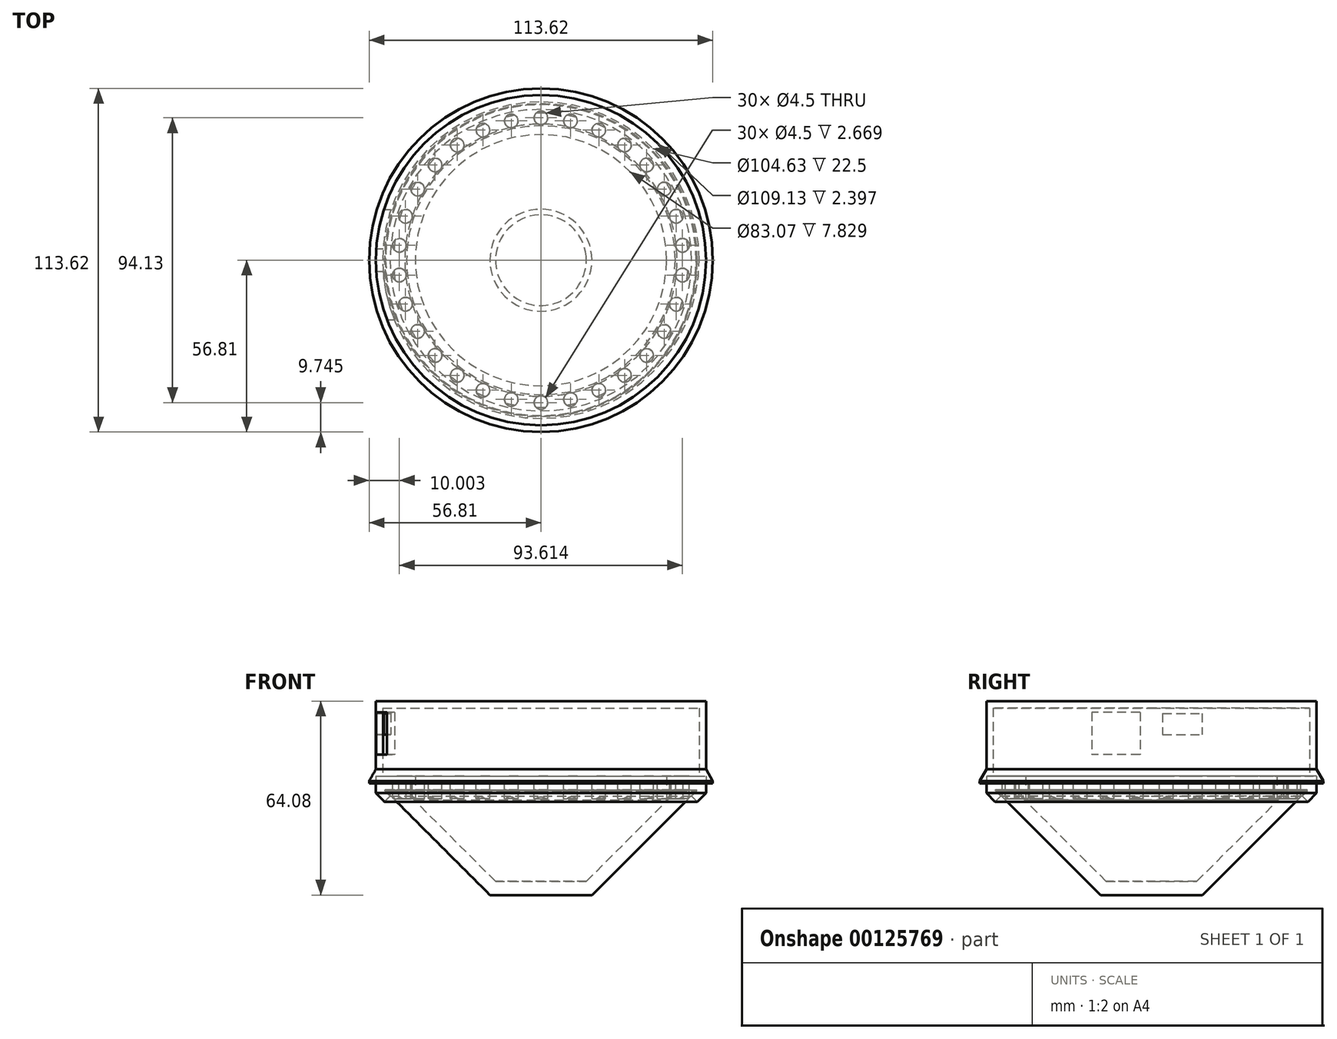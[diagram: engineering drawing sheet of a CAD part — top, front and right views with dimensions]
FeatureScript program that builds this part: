
annotation { "Feature Type Name" : "Feature", "Feature Type Description" : "" }
export const myFeature = defineFeature(function(context is Context, id is Id, definition is map)
    precondition{}
    {
        {
            var Q0;
            Q0=qCreatedBy(makeId("Front.planeOp"),FACE);
            var sketch = newSketch(context, id + "F0", { "sketchPlane" : qUnion([Q0])});
            skLineSegment(sketch, "E0", {"start": v(10, 0) * mm, "end": v(30, 20) * mm});
            skLineSegment(sketch, "E1", {"start": v(30, 20) * mm, "end": v(34.24, 20) * mm});
            skLineSegment(sketch, "E2", {"start": v(34.24, 20) * mm, "end": v(14.24, 0) * mm});
            skLineSegment(sketch, "E3", {"start": v(14.24, 0) * mm, "end": v(10, 0) * mm});
            skLineSegment(sketch, "E4", {"start": v(0, 0) * mm, "end": v(0, 45.27) * mm, "construction": true});
            skLineSegment(sketch, "E5", {"start": v(10, 0) * mm, "end": v(0, 0) * mm});
            skLineSegment(sketch, "E6", {"start": v(14.24, 0) * mm, "end": v(11.24, -3) * mm});
            skLineSegment(sketch, "E7", {"start": v(11.24, -3) * mm, "end": v(0, -3) * mm});
            skLineSegment(sketch, "E8", {"start": v(0, -3) * mm, "end": v(0, 0) * mm});
            skSolve(sketch);
        }
        {
            var Q0;
            Q0=makeQuery(id+"F0.imprint","IMPRINT",FACE,{"disambiguationData":[TD([[makeQuery(id+"F0.imprint","IMPRINT",EDGE,{"derivedFrom":sQuery(id+"F0.wireOp",EDGE,"E0")}),-1.0]])]});
            var Q1;
            Q1=makeQuery(id+"F0.imprint","IMPRINT",FACE,{"disambiguationData":[TD([[makeQuery(id+"F0.imprint","IMPRINT",EDGE,{"derivedFrom":sQuery(id+"F0.wireOp",EDGE,"E3")}),1.0]])]});
            var Q2;
            Q2=sQuery(id+"F0.wireOp",EDGE,"E4");
            revolve(context, id + "F1", {"entities" : qUnion([Q0, Q1]), "axis" : qUnion([Q2]), "revolveType" : RevolveType.FULL});
        }
        {
            var Q0;
            Q0=qCreatedBy(makeId("Front.planeOp"),FACE);
            var sketch = newSketch(context, id + "F2", { "sketchPlane" : qUnion([Q0])});
            skLineSegment(sketch, "E9.0", {"start": v(34.24, 20) * mm, "end": v(-34.24, 20) * mm});
            skLineSegment(sketch, "E10", {"start": v(34.38, 20.14) * mm, "end": v(34.32, 19.92) * mm});
            skLineSegment(sketch, "E11", {"start": v(34.32, 19.92) * mm, "end": v(33.23, 18.81) * mm});
            skLineSegment(sketch, "E12", {"start": v(33.23, 18.81) * mm, "end": v(34.5, 17.58) * mm});
            skLineSegment(sketch, "E13", {"start": v(34.5, 17.58) * mm, "end": v(36.38, 19.5) * mm});
            skLineSegment(sketch, "E14", {"start": v(36.38, 19.5) * mm, "end": v(36.38, 23.22) * mm});
            skLineSegment(sketch, "E15", {"start": v(36.38, 23.22) * mm, "end": v(27.7, 23.22) * mm});
            skLineSegment(sketch, "E16", {"start": v(27.7, 23.22) * mm, "end": v(27.7, 18) * mm});
            skLineSegment(sketch, "E17", {"start": v(27.7, 18) * mm, "end": v(29.61, 20.14) * mm});
            skLineSegment(sketch, "E18", {"start": v(29.61, 20.14) * mm, "end": v(34.38, 20.14) * mm});
            skSolve(sketch);
        }
        {
            var Q0;
            Q0=qCreatedBy(makeId("Front.planeOp"),FACE);
            var sketch = newSketch(context, id + "F3", { "sketchPlane" : qUnion([Q0])});
            skLineSegment(sketch, "E19", {"start": v(0, 0) * mm, "end": v(0, 38.08) * mm, "construction": true});
            skSolve(sketch);
        }
        {
            var Q0;
            Q0=makeQuery(id+"F2.imprint","IMPRINT",FACE,{"disambiguationData":[TD([[makeQuery(id+"F2.imprint","IMPRINT",EDGE,{"derivedFrom":sQuery(id+"F2.wireOp",EDGE,"E10")}),1.0]])]});
            var Q1;
            {var subQ0=sQuery(id+"F2.wireOp",EDGE,"E16");var subQ1=sQuery(id+"F2.wireOp",EDGE,"E9.0");var subQ2=makeQuery(id+"F2.imprint","INTERSECT",VERTEX,{"derivedFrom":[subQ1,subQ0]});Q1=makeQuery(id+"F2.imprint","IMPRINT",FACE,{"disambiguationData":[TD([[makeQuery(id+"F2.imprint","IMPRINT",EDGE,{"disambiguationData":[TD([[subQ2,1.0]])],"derivedFrom":subQ1}),1.0]])]});}
            var Q2;
            Q2=sQuery(id+"F3.wireOp",EDGE,"E19");
            revolve(context, id + "F4", {"entities" : qUnion([Q0, Q1]), "axis" : qUnion([Q2]), "revolveType" : RevolveType.FULL});
        }
        {
            var Q0;
            Q0=makeQuery(id+"F4.opRevolve","SWEPT_FACE",FACE,{"disambiguationData":[OSD([sQuery(id+"F2.wireOp",EDGE,"E15")])]});
            var sketch = newSketch(context, id + "F5", { "sketchPlane" : qUnion([Q0])});
            skCircle(sketch, "E20", {"center": v(0, 31.38) * mm, "radius": 1.5 * mm});
            skLineSegment(sketch, "E21", {"start": v(0, 36.38) * mm, "end": v(0, 27.7) * mm, "construction": true});
            skCircle(sketch, "E22.1.0", {"center": v(-6.52, 30.7) * mm, "radius": 1.5 * mm});
            skCircle(sketch, "E22.2.0", {"center": v(-12.76, 28.66) * mm, "radius": 1.5 * mm});
            skCircle(sketch, "E22.3.0", {"center": v(-18.44, 25.38) * mm, "radius": 1.5 * mm});
            skCircle(sketch, "E22.4.0", {"center": v(-23.32, 21) * mm, "radius": 1.5 * mm});
            skCircle(sketch, "E22.5.0", {"center": v(-27.17, 15.69) * mm, "radius": 1.5 * mm});
            skCircle(sketch, "E22.6.0", {"center": v(-29.84, 9.7) * mm, "radius": 1.5 * mm});
            skCircle(sketch, "E22.7.0", {"center": v(-31.2, 3.28) * mm, "radius": 1.5 * mm});
            skCircle(sketch, "E22.8.0", {"center": v(-31.2, -3.28) * mm, "radius": 1.5 * mm});
            skCircle(sketch, "E22.9.0", {"center": v(-29.84, -9.7) * mm, "radius": 1.5 * mm});
            skCircle(sketch, "E22.10.0", {"center": v(-27.17, -15.69) * mm, "radius": 1.5 * mm});
            skCircle(sketch, "E22.11.0", {"center": v(-23.32, -21) * mm, "radius": 1.5 * mm});
            skCircle(sketch, "E22.12.0", {"center": v(-18.44, -25.38) * mm, "radius": 1.5 * mm});
            skCircle(sketch, "E22.13.0", {"center": v(-12.76, -28.66) * mm, "radius": 1.5 * mm});
            skCircle(sketch, "E22.14.0", {"center": v(-6.52, -30.7) * mm, "radius": 1.5 * mm});
            skCircle(sketch, "E22.15.0", {"center": v(0, -31.38) * mm, "radius": 1.5 * mm});
            skCircle(sketch, "E22.16.0", {"center": v(6.52, -30.7) * mm, "radius": 1.5 * mm});
            skCircle(sketch, "E22.17.0", {"center": v(12.76, -28.66) * mm, "radius": 1.5 * mm});
            skCircle(sketch, "E22.18.0", {"center": v(18.44, -25.38) * mm, "radius": 1.5 * mm});
            skCircle(sketch, "E22.19.0", {"center": v(23.32, -21) * mm, "radius": 1.5 * mm});
            skCircle(sketch, "E22.20.0", {"center": v(27.17, -15.69) * mm, "radius": 1.5 * mm});
            skCircle(sketch, "E22.21.0", {"center": v(29.84, -9.7) * mm, "radius": 1.5 * mm});
            skCircle(sketch, "E22.22.0", {"center": v(31.2, -3.28) * mm, "radius": 1.5 * mm});
            skCircle(sketch, "E22.23.0", {"center": v(31.2, 3.28) * mm, "radius": 1.5 * mm});
            skCircle(sketch, "E22.24.0", {"center": v(29.84, 9.7) * mm, "radius": 1.5 * mm});
            skCircle(sketch, "E22.25.0", {"center": v(27.17, 15.69) * mm, "radius": 1.5 * mm});
            skCircle(sketch, "E22.26.0", {"center": v(23.32, 21) * mm, "radius": 1.5 * mm});
            skCircle(sketch, "E22.27.0", {"center": v(18.44, 25.38) * mm, "radius": 1.5 * mm});
            skCircle(sketch, "E22.28.0", {"center": v(12.76, 28.66) * mm, "radius": 1.5 * mm});
            skCircle(sketch, "E22.29.0", {"center": v(6.52, 30.7) * mm, "radius": 1.5 * mm});
            skPoint(sketch, "E22.center", {"position": v(0, 0) * mm});
            skSolve(sketch);
        }
        {
            var Q0;
            Q0=makeQuery(id+"F5.imprint","IMPRINT",FACE,{"disambiguationData":[TD([[makeQuery(id+"F5.imprint","IMPRINT",EDGE,{"derivedFrom":sQuery(id+"F5.wireOp",EDGE,"E20")}),1.0]])]});
            var Q1;
            Q1=makeQuery(id+"F5.imprint","IMPRINT",FACE,{"disambiguationData":[TD([[makeQuery(id+"F5.imprint","IMPRINT",EDGE,{"derivedFrom":sQuery(id+"F5.wireOp",EDGE,"E22.29.0")}),1.0]])]});
            var Q2;
            Q2=makeQuery(id+"F5.imprint","IMPRINT",FACE,{"disambiguationData":[TD([[makeQuery(id+"F5.imprint","IMPRINT",EDGE,{"derivedFrom":sQuery(id+"F5.wireOp",EDGE,"E22.28.0")}),1.0]])]});
            var Q3;
            Q3=makeQuery(id+"F5.imprint","IMPRINT",FACE,{"disambiguationData":[TD([[makeQuery(id+"F5.imprint","IMPRINT",EDGE,{"derivedFrom":sQuery(id+"F5.wireOp",EDGE,"E22.27.0")}),1.0]])]});
            var Q4;
            Q4=makeQuery(id+"F5.imprint","IMPRINT",FACE,{"disambiguationData":[TD([[makeQuery(id+"F5.imprint","IMPRINT",EDGE,{"derivedFrom":sQuery(id+"F5.wireOp",EDGE,"E22.26.0")}),1.0]])]});
            var Q5;
            Q5=makeQuery(id+"F5.imprint","IMPRINT",FACE,{"disambiguationData":[TD([[makeQuery(id+"F5.imprint","IMPRINT",EDGE,{"derivedFrom":sQuery(id+"F5.wireOp",EDGE,"E22.25.0")}),1.0]])]});
            var Q6;
            Q6=makeQuery(id+"F5.imprint","IMPRINT",FACE,{"disambiguationData":[TD([[makeQuery(id+"F5.imprint","IMPRINT",EDGE,{"derivedFrom":sQuery(id+"F5.wireOp",EDGE,"E22.23.0")}),1.0]])]});
            var Q7;
            Q7=makeQuery(id+"F5.imprint","IMPRINT",FACE,{"disambiguationData":[TD([[makeQuery(id+"F5.imprint","IMPRINT",EDGE,{"derivedFrom":sQuery(id+"F5.wireOp",EDGE,"E22.22.0")}),1.0]])]});
            var Q8;
            Q8=makeQuery(id+"F5.imprint","IMPRINT",FACE,{"disambiguationData":[TD([[makeQuery(id+"F5.imprint","IMPRINT",EDGE,{"derivedFrom":sQuery(id+"F5.wireOp",EDGE,"E22.21.0")}),1.0]])]});
            var Q9;
            Q9=makeQuery(id+"F5.imprint","IMPRINT",FACE,{"disambiguationData":[TD([[makeQuery(id+"F5.imprint","IMPRINT",EDGE,{"derivedFrom":sQuery(id+"F5.wireOp",EDGE,"E22.1.0")}),1.0]])]});
            var Q10;
            Q10=makeQuery(id+"F5.imprint","IMPRINT",FACE,{"disambiguationData":[TD([[makeQuery(id+"F5.imprint","IMPRINT",EDGE,{"derivedFrom":sQuery(id+"F5.wireOp",EDGE,"E22.2.0")}),1.0]])]});
            var Q11;
            Q11=makeQuery(id+"F5.imprint","IMPRINT",FACE,{"disambiguationData":[TD([[makeQuery(id+"F5.imprint","IMPRINT",EDGE,{"derivedFrom":sQuery(id+"F5.wireOp",EDGE,"E22.3.0")}),1.0]])]});
            var Q12;
            Q12=makeQuery(id+"F5.imprint","IMPRINT",FACE,{"disambiguationData":[TD([[makeQuery(id+"F5.imprint","IMPRINT",EDGE,{"derivedFrom":sQuery(id+"F5.wireOp",EDGE,"E22.4.0")}),1.0]])]});
            var Q13;
            Q13=makeQuery(id+"F5.imprint","IMPRINT",FACE,{"disambiguationData":[TD([[makeQuery(id+"F5.imprint","IMPRINT",EDGE,{"derivedFrom":sQuery(id+"F5.wireOp",EDGE,"E22.6.0")}),1.0]])]});
            var Q14;
            Q14=makeQuery(id+"F5.imprint","IMPRINT",FACE,{"disambiguationData":[TD([[makeQuery(id+"F5.imprint","IMPRINT",EDGE,{"derivedFrom":sQuery(id+"F5.wireOp",EDGE,"E22.7.0")}),1.0]])]});
            var Q15;
            Q15=makeQuery(id+"F5.imprint","IMPRINT",FACE,{"disambiguationData":[TD([[makeQuery(id+"F5.imprint","IMPRINT",EDGE,{"derivedFrom":sQuery(id+"F5.wireOp",EDGE,"E22.8.0")}),1.0]])]});
            var Q16;
            Q16=makeQuery(id+"F5.imprint","IMPRINT",FACE,{"disambiguationData":[TD([[makeQuery(id+"F5.imprint","IMPRINT",EDGE,{"derivedFrom":sQuery(id+"F5.wireOp",EDGE,"E22.9.0")}),1.0]])]});
            var Q17;
            Q17=makeQuery(id+"F5.imprint","IMPRINT",FACE,{"disambiguationData":[TD([[makeQuery(id+"F5.imprint","IMPRINT",EDGE,{"derivedFrom":sQuery(id+"F5.wireOp",EDGE,"E22.10.0")}),1.0]])]});
            var Q18;
            Q18=makeQuery(id+"F5.imprint","IMPRINT",FACE,{"disambiguationData":[TD([[makeQuery(id+"F5.imprint","IMPRINT",EDGE,{"derivedFrom":sQuery(id+"F5.wireOp",EDGE,"E22.11.0")}),1.0]])]});
            var Q19;
            Q19=makeQuery(id+"F5.imprint","IMPRINT",FACE,{"disambiguationData":[TD([[makeQuery(id+"F5.imprint","IMPRINT",EDGE,{"derivedFrom":sQuery(id+"F5.wireOp",EDGE,"E22.12.0")}),1.0]])]});
            var Q20;
            Q20=makeQuery(id+"F5.imprint","IMPRINT",FACE,{"disambiguationData":[TD([[makeQuery(id+"F5.imprint","IMPRINT",EDGE,{"derivedFrom":sQuery(id+"F5.wireOp",EDGE,"E22.13.0")}),1.0]])]});
            var Q21;
            Q21=makeQuery(id+"F5.imprint","IMPRINT",FACE,{"disambiguationData":[TD([[makeQuery(id+"F5.imprint","IMPRINT",EDGE,{"derivedFrom":sQuery(id+"F5.wireOp",EDGE,"E22.5.0")}),1.0]])]});
            var Q22;
            Q22=makeQuery(id+"F5.imprint","IMPRINT",FACE,{"disambiguationData":[TD([[makeQuery(id+"F5.imprint","IMPRINT",EDGE,{"derivedFrom":sQuery(id+"F5.wireOp",EDGE,"E22.14.0")}),1.0]])]});
            var Q23;
            Q23=makeQuery(id+"F5.imprint","IMPRINT",FACE,{"disambiguationData":[TD([[makeQuery(id+"F5.imprint","IMPRINT",EDGE,{"derivedFrom":sQuery(id+"F5.wireOp",EDGE,"E22.15.0")}),1.0]])]});
            var Q24;
            Q24=makeQuery(id+"F5.imprint","IMPRINT",FACE,{"disambiguationData":[TD([[makeQuery(id+"F5.imprint","IMPRINT",EDGE,{"derivedFrom":sQuery(id+"F5.wireOp",EDGE,"E22.16.0")}),1.0]])]});
            var Q25;
            Q25=makeQuery(id+"F5.imprint","IMPRINT",FACE,{"disambiguationData":[TD([[makeQuery(id+"F5.imprint","IMPRINT",EDGE,{"derivedFrom":sQuery(id+"F5.wireOp",EDGE,"E22.17.0")}),1.0]])]});
            var Q26;
            Q26=makeQuery(id+"F5.imprint","IMPRINT",FACE,{"disambiguationData":[TD([[makeQuery(id+"F5.imprint","IMPRINT",EDGE,{"derivedFrom":sQuery(id+"F5.wireOp",EDGE,"E22.18.0")}),1.0]])]});
            var Q27;
            Q27=makeQuery(id+"F5.imprint","IMPRINT",FACE,{"disambiguationData":[TD([[makeQuery(id+"F5.imprint","IMPRINT",EDGE,{"derivedFrom":sQuery(id+"F5.wireOp",EDGE,"E22.19.0")}),1.0]])]});
            var Q28;
            Q28=makeQuery(id+"F5.imprint","IMPRINT",FACE,{"disambiguationData":[TD([[makeQuery(id+"F5.imprint","IMPRINT",EDGE,{"derivedFrom":sQuery(id+"F5.wireOp",EDGE,"E22.20.0")}),1.0]])]});
            var Q29;
            Q29=makeQuery(id+"F5.imprint","IMPRINT",FACE,{"disambiguationData":[TD([[makeQuery(id+"F5.imprint","IMPRINT",EDGE,{"derivedFrom":sQuery(id+"F5.wireOp",EDGE,"E22.24.0")}),1.0]])]});
            extrude(context, id + "F6", {"entities" : qUnion([Q0, Q1, Q2, Q3, Q4, Q5, Q6, Q7, Q8, Q9, Q10, Q11, Q12, Q13, Q14, Q15, Q16, Q17, Q18, Q19, Q20, Q21, Q22, Q23, Q24, Q25, Q26, Q27, Q28, Q29]), "operationType" : NewBodyOperationType.REMOVE, "oppositeDirection" : true, "depth" : 5 * mm});
        }
        {
            var Q0;
            Q0=qCreatedBy(makeId("Front.planeOp"),FACE);
            var sketch = newSketch(context, id + "F7", { "sketchPlane" : qUnion([Q0])});
            skLineSegment(sketch, "E23.0", {"start": v(36.38, 23.22) * mm, "end": v(-36.38, 23.22) * mm});
            skLineSegment(sketch, "E24", {"start": v(36.38, 23.22) * mm, "end": v(36.38, 39.72) * mm});
            skLineSegment(sketch, "E25", {"start": v(36.38, 39.72) * mm, "end": v(0, 39.72) * mm});
            skLineSegment(sketch, "E26", {"start": v(0, 39.72) * mm, "end": v(0, 38.22) * mm});
            skLineSegment(sketch, "E27", {"start": v(0, 38.22) * mm, "end": v(34.88, 38.22) * mm});
            skLineSegment(sketch, "E28", {"start": v(34.88, 38.22) * mm, "end": v(34.88, 23.22) * mm});
            skLineSegment(sketch, "E29", {"start": v(34.88, 23.22) * mm, "end": v(36.38, 23.22) * mm});
            skLineSegment(sketch, "E30", {"start": v(36.38, 24.72) * mm, "end": v(37.88, 22.12) * mm});
            skLineSegment(sketch, "E31", {"start": v(37.88, 22.12) * mm, "end": v(37.88, 21.62) * mm});
            skLineSegment(sketch, "E32", {"start": v(37.88, 21.62) * mm, "end": v(36.38, 21.62) * mm});
            skLineSegment(sketch, "E33", {"start": v(36.38, 21.62) * mm, "end": v(36.38, 23.22) * mm});
            skSolve(sketch);
        }
        {
            var Q0;
            {var subQ0=sQuery(id+"F7.wireOp",EDGE,"E25");Q0=makeQuery(id+"F7.imprint","IMPRINT",FACE,{"disambiguationData":[TD([[makeQuery(id+"F7.imprint","IMPRINT",EDGE,{"derivedFrom":subQ0}),1.0]])]});}
            var Q1;
            {var subQ0=sQuery(id+"F7.wireOp",EDGE,"E30");Q1=makeQuery(id+"F7.imprint","IMPRINT",FACE,{"disambiguationData":[TD([[makeQuery(id+"F7.imprint","IMPRINT",EDGE,{"derivedFrom":subQ0}),-1.0]])]});}
            var Q2;
            Q2=sQuery(id+"F3.wireOp",EDGE,"E19");
            revolve(context, id + "F8", {"entities" : qUnion([Q0, Q1]), "axis" : qUnion([Q2]), "revolveType" : RevolveType.FULL});
        }
        {
            var Q0;
            Q0=makeQuery(id+"F8.opRevolve","SWEPT_BODY",BODY,{"disambiguationData":[OSD([sQuery(id+"F7.wireOp",EDGE,"E24"),sQuery(id+"F7.wireOp",EDGE,"E25"),sQuery(id+"F7.wireOp",EDGE,"E26"),sQuery(id+"F7.wireOp",EDGE,"E27"),sQuery(id+"F7.wireOp",EDGE,"E28"),sQuery(id+"F7.wireOp",EDGE,"E29"),sQuery(id+"F7.wireOp",EDGE,"E30"),sQuery(id+"F7.wireOp",EDGE,"E31"),sQuery(id+"F7.wireOp",EDGE,"E32"),sQuery(id+"F7.wireOp",EDGE,"E33")])]});
            var Q1;
            Q1=makeQuery(id+"F4.opRevolve","SWEPT_BODY",BODY,{"disambiguationData":[OSD([sQuery(id+"F2.wireOp",EDGE,"E10"),sQuery(id+"F2.wireOp",EDGE,"E11"),sQuery(id+"F2.wireOp",EDGE,"E12"),sQuery(id+"F2.wireOp",EDGE,"E13"),sQuery(id+"F2.wireOp",EDGE,"E14"),sQuery(id+"F2.wireOp",EDGE,"E15"),sQuery(id+"F2.wireOp",EDGE,"E16"),sQuery(id+"F2.wireOp",EDGE,"E17"),sQuery(id+"F2.wireOp",EDGE,"E18")])]});
            var Q2;
            Q2=makeQuery(id+"F1.opRevolve","SWEPT_BODY",BODY,{"disambiguationData":[OSD([sQuery(id+"F0.wireOp",EDGE,"E0"),sQuery(id+"F0.wireOp",EDGE,"E1"),sQuery(id+"F0.wireOp",EDGE,"E2"),sQuery(id+"F0.wireOp",EDGE,"E5"),sQuery(id+"F0.wireOp",EDGE,"E6"),sQuery(id+"F0.wireOp",EDGE,"E7"),sQuery(id+"F0.wireOp",EDGE,"E8")])]});
            var Q3;
            Q3=sQuery(id+"F3.wireOp",VERTEX,"E19.start");
            transform(context, id + "F9", {"entities" : qUnion([Q0, Q1, Q2]), "transformType" : TransformType.SCALE_UNIFORMLY, "scale" : 1.5, "scalePoint" : qUnion([Q3]), "makeCopy" : false});
        }
        {
            var Q0;
            Q0=qCreatedBy(makeId("Right.planeOp"),FACE);
            cPlane(context, id + "F10", {"entities" : qUnion([Q0]), "cplaneType" : CPlaneType.OFFSET, "offset" : 60 * mm, "oppositeDirection" : true, "width" : 150 * mm, "height" : 150 * mm});
        }
        {
            var Q0;
            Q0=qCreatedBy(id+"F10.planeOp",FACE);
            var sketch = newSketch(context, id + "F11", { "sketchPlane" : qUnion([Q0])});
            skLineSegment(sketch, "E34.bottom", {"start": v(-19.77, 55.93) * mm, "end": v(-3.77, 55.93) * mm});
            skLineSegment(sketch, "E34.left", {"start": v(-3.77, 41.93) * mm, "end": v(-3.77, 55.93) * mm});
            skLineSegment(sketch, "E34.right", {"start": v(-19.77, 55.93) * mm, "end": v(-19.77, 41.93) * mm});
            skLineSegment(sketch, "E35.bottom", {"start": v(16.66, 55.56) * mm, "end": v(3.66, 55.56) * mm});
            skLineSegment(sketch, "E35.top", {"start": v(16.66, 48.56) * mm, "end": v(3.66, 48.56) * mm});
            skLineSegment(sketch, "E35.left", {"start": v(16.66, 55.56) * mm, "end": v(16.66, 48.56) * mm});
            skLineSegment(sketch, "E35.right", {"start": v(3.66, 55.56) * mm, "end": v(3.66, 48.56) * mm});
            skLineSegment(sketch, "E36", {"start": v(-19.77, 41.93) * mm, "end": v(-3.77, 41.93) * mm});
            skSolve(sketch);
        }
        {
            var Q0;
            Q0=makeQuery(id+"F11.imprint","IMPRINT",FACE,{"disambiguationData":[TD([[makeQuery(id+"F11.imprint","IMPRINT",EDGE,{"derivedFrom":sQuery(id+"F11.wireOp",EDGE,"E34.bottom")}),-1.0]])]});
            var Q1;
            Q1=makeQuery(id+"F11.imprint","IMPRINT",FACE,{"disambiguationData":[TD([[makeQuery(id+"F11.imprint","IMPRINT",EDGE,{"derivedFrom":sQuery(id+"F11.wireOp",EDGE,"E35.bottom")}),1.0]])]});
            extrude(context, id + "F12", {"entities" : qUnion([Q0, Q1]), "operationType" : NewBodyOperationType.REMOVE, "depth" : 25 * mm});
        }
    });
